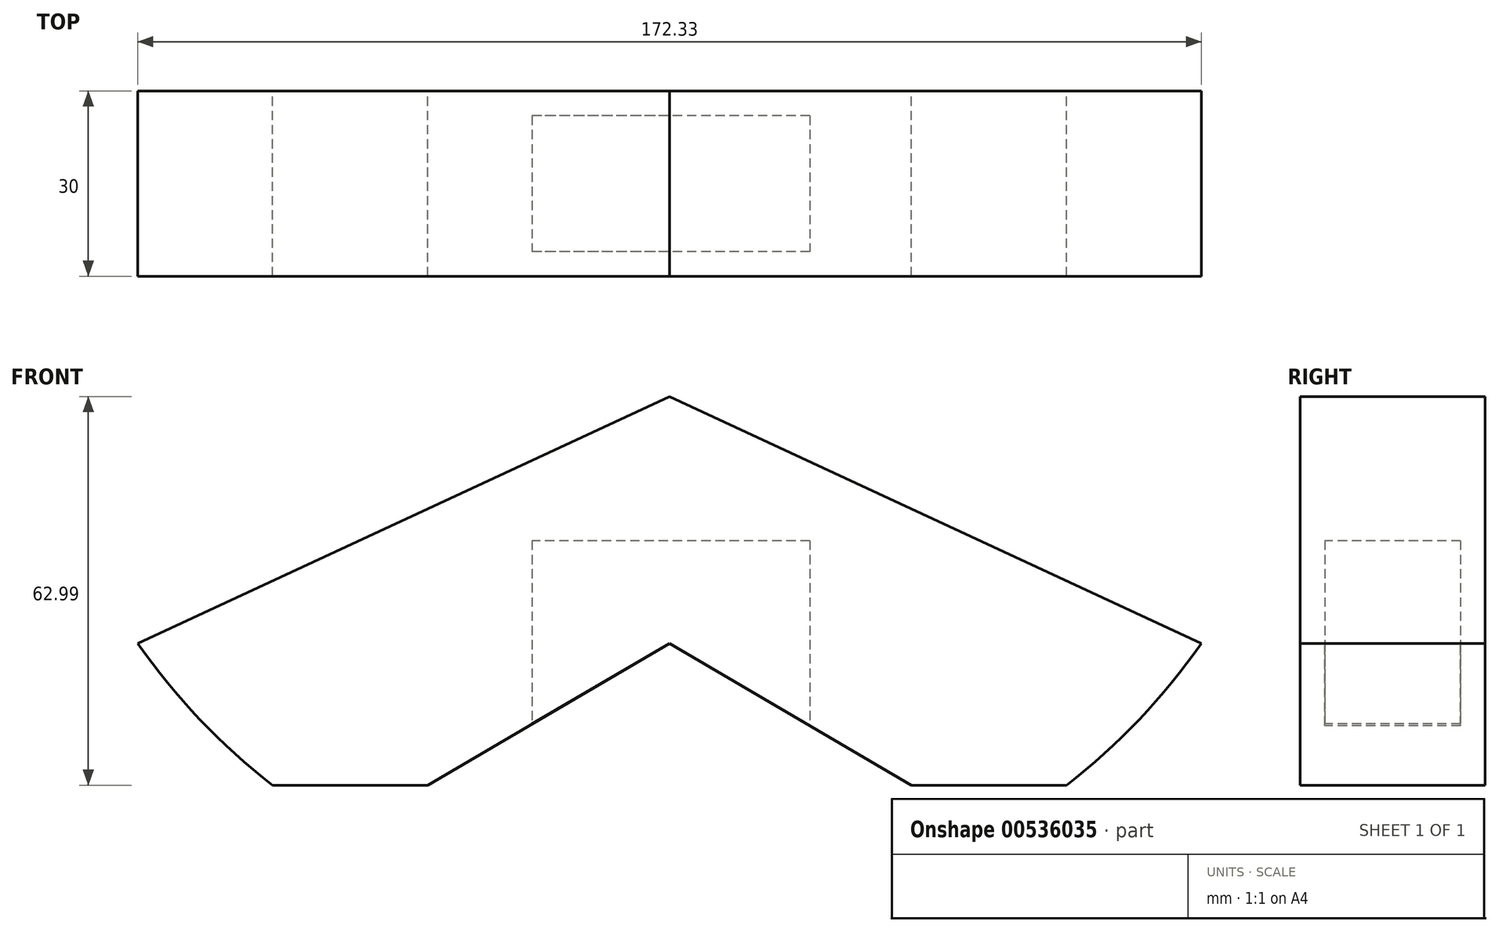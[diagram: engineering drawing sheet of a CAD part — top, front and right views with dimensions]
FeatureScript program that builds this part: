
annotation { "Feature Type Name" : "Feature", "Feature Type Description" : "" }
export const myFeature = defineFeature(function(context is Context, id is Id, definition is map)
    precondition{}
    {
        {
            var Q0;
            Q0=qCreatedBy(makeId("Front.planeOp"),FACE);
            var sketch = newSketch(context, id + "F0", { "sketchPlane" : qUnion([Q0])});
            skCircle(sketch, "E0", {"center": v(3.8, 45) * mm, "radius": 105 * mm});
            skLineSegment(sketch, "E1", {"start": v(3.8, 45) * mm, "end": v(3.8, 150) * mm});
            skLineSegment(sketch, "E2", {"start": v(3.8, 45) * mm, "end": v(3.8, 25) * mm});
            skLineSegment(sketch, "E3", {"start": v(3.8, 25) * mm, "end": v(106.88, 25) * mm});
            skLineSegment(sketch, "E4", {"start": v(3.8, 25) * mm, "end": v(-99.27, 25) * mm});
            skLineSegment(sketch, "E5", {"start": v(3.8, -15) * mm, "end": v(-48.81, -45.87) * mm});
            skLineSegment(sketch, "E6", {"start": v(56.42, -45.87) * mm, "end": v(3.8, -15) * mm});
            skLineSegment(sketch, "E7", {"start": v(-60.51, -38) * mm, "end": v(-35.4, -38) * mm});
            skLineSegment(sketch, "E8", {"start": v(43, -38) * mm, "end": v(68.12, -38) * mm});
            skCircle(sketch, "E9.0", {"center": v(3.8, 45) * mm, "radius": 111.35 * mm});
            skLineSegment(sketch, "E10", {"start": v(-82.36, -15) * mm, "end": v(3.8, 25) * mm});
            skLineSegment(sketch, "E11", {"start": v(3.8, 25) * mm, "end": v(89.97, -15) * mm});
            skLineSegment(sketch, "E12", {"start": v(-35.4, -38) * mm, "end": v(43, -38) * mm});
            skLineSegment(sketch, "E13", {"start": v(3.8, -15) * mm, "end": v(3.8, 0) * mm});
            skSolve(sketch);
        }
        {
            var Q0;
            {var subQ4=sQuery(id+"F0.wireOp",EDGE,"E7");Q0=makeQuery(id+"F0.imprint","IMPRINT",FACE,{"disambiguationData":[TD([[makeQuery(id+"F0.imprint","IMPRINT",EDGE,{"derivedFrom":subQ4}),1.0]])]});}
            extrude(context, id + "F1", {"entities" : qUnion([Q0]), "depth" : 30 * mm, "offsetDistance" : 25.4 * mm});
        }
        {
            var Q0;
            {var subQ0=sQuery(id+"F0.wireOp",EDGE,"E8");var subQ1=sQuery(id+"F0.wireOp",EDGE,"E7");Q0=makeQuery(id+"FJSeFZwpdwuf3KU_0.boolean.opBoolean","MERGE",FACE,{"derivedFrom":[makeQuery(id+"F1.opExtrude","SWEPT_FACE",FACE,{"disambiguationData":[OSD([subQ1])]}),makeQuery(id+"F1.opExtrude","SWEPT_FACE",FACE,{"disambiguationData":[OSD([subQ0])]}),makeQuery(id+"FJSeFZwpdwuf3KU_0.opExtrude","SWEPT_FACE",FACE,{"disambiguationData":[OSD([subQ1,subQ0,sQuery(id+"F0.wireOp",EDGE,"E12")])]})]});}
            var sketch = newSketch(context, id + "F2", { "sketchPlane" : qUnion([Q0])});
            skLineSegment(sketch, "E14", {"start": v(0, 0) * mm, "end": v(0, 15) * mm});
            skPoint(sketch, "E15.middle", {"position": v(0, 15) * mm});
            skLineSegment(sketch, "E16.bottom", {"start": v(26.54, 4) * mm, "end": v(-18.46, 4) * mm});
            skLineSegment(sketch, "E16.top", {"start": v(26.54, 26) * mm, "end": v(-18.46, 26) * mm});
            skLineSegment(sketch, "E16.left", {"start": v(26.54, 4) * mm, "end": v(26.54, 26) * mm});
            skLineSegment(sketch, "E16.right", {"start": v(-18.46, 4) * mm, "end": v(-18.46, 26) * mm});
            skPoint(sketch, "E16.middle", {"position": v(4.04, 15) * mm});
            skSolve(sketch);
        }
        {
            var Q0;
            Q0=makeQuery(id+"F2.imprint","IMPRINT",FACE,{"disambiguationData":[TD([[makeQuery(id+"F2.imprint","IMPRINT",EDGE,{"derivedFrom":sQuery(id+"F2.wireOp",EDGE,"E16.top")}),1.0]])]});
            extrude(context, id + "F3", {"entities" : qUnion([Q0]), "operationType" : NewBodyOperationType.REMOVE, "oppositeDirection" : true, "depth" : 39.62 * mm, "offsetDistance" : 25.4 * mm});
        }
    });
